# Revit family: vl-16_18(e)u(r)(h)3_50Hz
name_source: partatom
category: 機械設備
units: mm (PartAtom-declared; Revit-internal decimal feet)

## family parameters
OmniClass タイトル = Centrifugal Fans
OmniClass 番号 = 23.75.35.17.27
パーツ タイプ = 標準
ロード時にボイドで切り取り = いいえ
丸型コネクタ寸法 = 直径を使用
作業面ベース = いいえ
共有 = いいえ
常に垂直 = はい
部屋計算ポイント = いいえ

## types (4) — shared parameters
Clearance Bottom = 101
Clearance Left = 50  [stored 0.164042 ft]
Clearance Right = 50  [stored 0.164042 ft]
Clearance Top = 61
Depth = 185  [stored 0.606955 ft]
Duct_Pitch = 350  [stored 1.14829 ft]
IfcExportAs = IfcFanType
IfcExportType = CENTRIFUGALBACKWARDINCLINEDCURVED
MAX静圧 = 0.0 Pa
MID静圧 = 0.0 Pa
MID風量 = 0.0 m³/h
MIN静圧 = 0.0 Pa
OmniClassCode = 23-33 31 19 13 13
URL = https://www.mitsubishielectric.co.jp
Uniclass2015Code = Pr_65_67_29_89
Uniclass2015Title = Twin centrifugal fans
Uniclass2015Version = Systems v1.9
W1 = 185  [stored 0.606955 ft]
マテリアル = 合成樹脂(白)
メンテナンススペース = はい
仕様書バージョン = Version1.0
企業コード = 108420
分類コード = 50052504100030
周波数 = 50 Hz
極数 = 2
法定耐用年数 = 15
相 = 1
積算_科目 = 2 換気設備
製品リリース年月 = 2019年5月16日
製品出荷対象 = 国内
製造元 = 三菱電機株式会社
設置方法 = 壁付
説明 = 換気空清機ロスナイ 準寒冷･温暖地仕様 壁掛2パイプ取付タイプ
負荷分類 = 3_ファン類
運転質量 = 0.00 kg
電動機出力 = 0 W
電圧 = 100 V
zero-valued in all types: Clearance Back, Clearance Front

## per-type parameters (varying)
| type | Duct_H | EAサイズ_D | Height | MAX風量 | MIN風量 | SAサイズ_D | Width | ダクト径 | 価格 | 消費電力 | 温度交換効率 | 製品質量 | 質量 |
| VL-18EUH3 | 25  [stored 0.082021 ft] | 100  [stored 0.328084 ft] | 285 | 55.0 m³/h | 0.0 m³/h | 100  [stored 0.328084 ft] | 620 | 100 mm | 78400 $ | 22 W | 65.00% | 7.00 kg | 8.40 kg |
| VL-18URH3 | 25  [stored 0.082021 ft] | 100  [stored 0.328084 ft] | 285 | 55.0 m³/h | 0.0 m³/h | 100  [stored 0.328084 ft] | 620 | 100 mm | 90200 $ | 22 W | 65.00% | 7.00 kg | 8.40 kg |
| VL-16U3 | 15  [stored 0.0492126 ft] | 75 | 265 | 93.0 m³/h | 55.0 m³/h | 75 | 550 | 75 mm | 64500 $ | 33 W | 70.00% | 6.00 kg | 7.20 kg |
| VL-16EU3 | 15  [stored 0.0492126 ft] | 75 | 265 | 93.0 m³/h | 55.0 m³/h | 75 | 550 | 75 mm | 69700 $ | 33 W | 70.00% | 6.00 kg | 7.20 kg |

note: column(s) folded — value = type name in every type: モデル

note: [stored X ft] marks values corroborated as IEEE doubles in the binary element streams (Revit-internal decimal feet)
